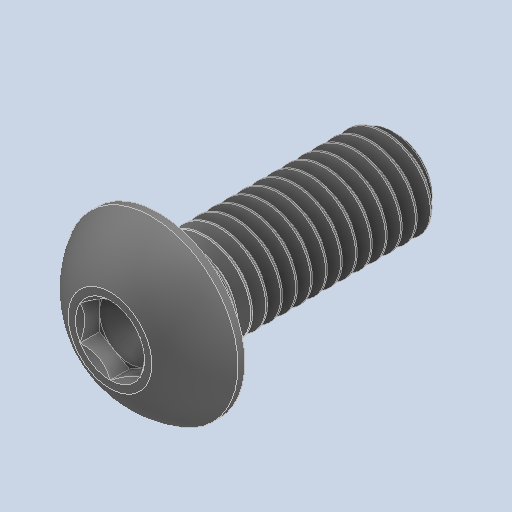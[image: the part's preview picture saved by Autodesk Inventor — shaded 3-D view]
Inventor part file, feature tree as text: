
AUTODESK INVENTOR PART (.ipt)
format: ipt  version: 2023.2 (Build 272271000, 271)  size: 549,376 bytes
history: native  units: in
note: dims shown in document units (in); Inventor stores cm internally (conversion verified against a paired STEP export)
features: revolve x1
ambient origin geometry x8: Origin, YZ Plane, XZ Plane, XY Plane, X Axis, Y Axis, Z Axis, Center Point
bodies: Solid1 (feature_tree)
feature tree (1):
  revolve  "Revolve2"  [1 undecoded]
note: 1 required parameter value undecoded (feature->parameter linkage not recoverable at this tier; creation-order binding heuristic only, values carry confidence <= 0.55)
